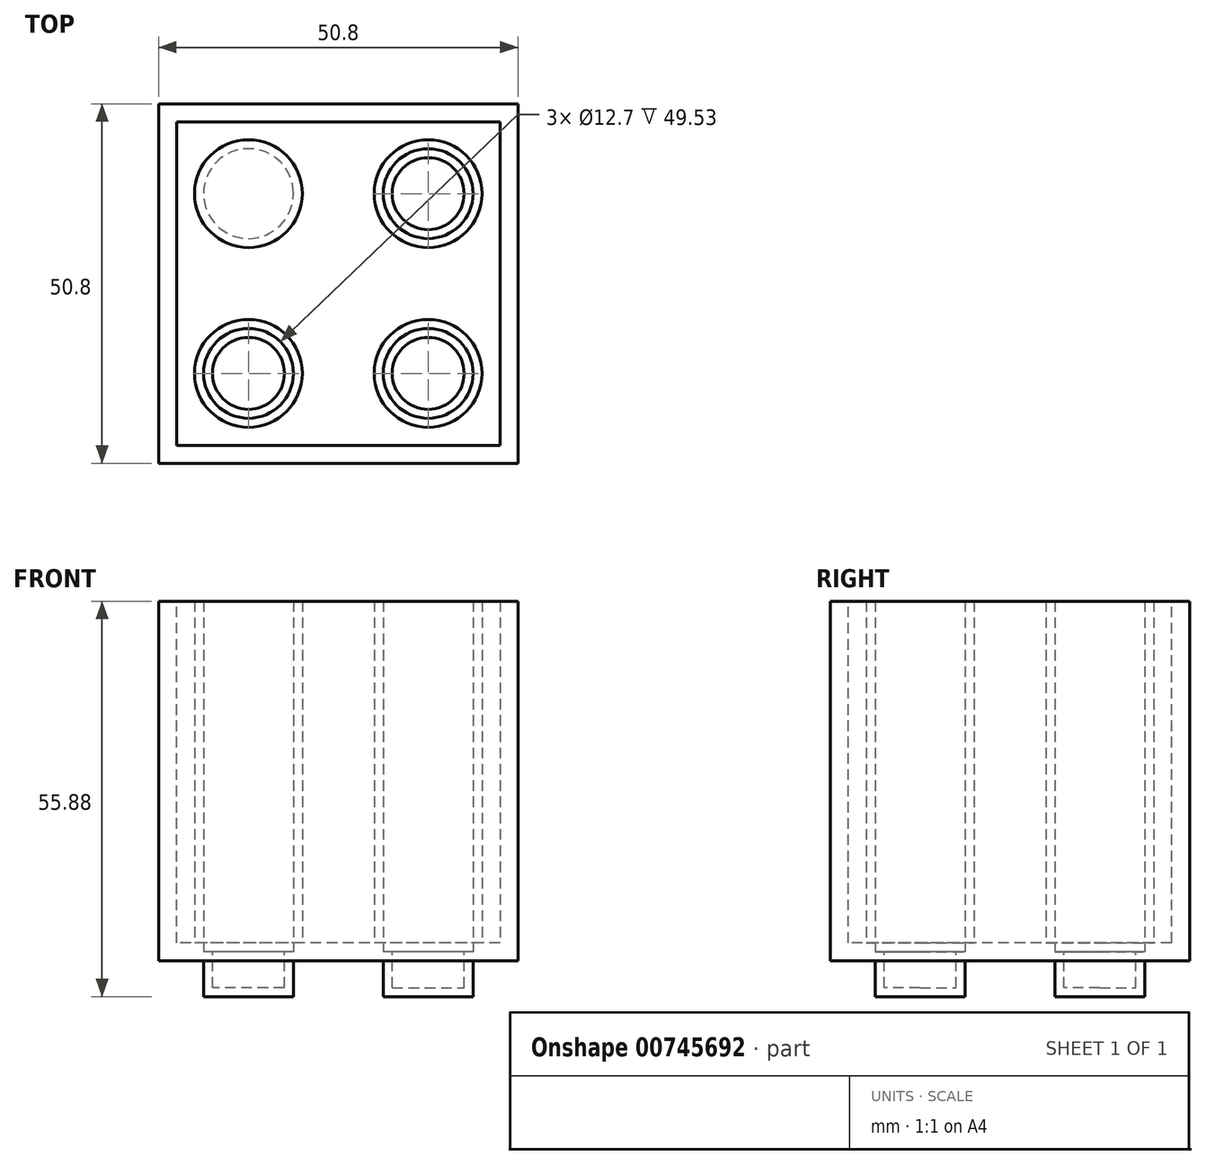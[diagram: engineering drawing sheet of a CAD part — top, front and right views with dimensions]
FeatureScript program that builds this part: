
annotation { "Feature Type Name" : "Feature", "Feature Type Description" : "" }
export const myFeature = defineFeature(function(context is Context, id is Id, definition is map)
    precondition{}
    {
        {
            var Q0;
            Q0=qCreatedBy(makeId("Front.planeOp"),FACE);
            var sketch = newSketch(context, id + "F0", { "sketchPlane" : qUnion([Q0])});
            skLineSegment(sketch, "E0", {"start": v(0, 0) * mm, "end": v(0, 50.8) * mm});
            skLineSegment(sketch, "E1", {"start": v(0, 50.8) * mm, "end": v(50.8, 50.8) * mm});
            skLineSegment(sketch, "E2", {"start": v(50.8, 50.8) * mm, "end": v(50.8, 0) * mm});
            skLineSegment(sketch, "E3", {"start": v(50.8, 0) * mm, "end": v(0, 0) * mm});
            skSolve(sketch);
        }
        {
            var Q0;
            Q0=makeQuery(id+"F0.imprint","IMPRINT",FACE,{"disambiguationData":[TD([[makeQuery(id+"F0.imprint","IMPRINT",EDGE,{"derivedFrom":sQuery(id+"F0.wireOp",EDGE,"E0")}),-1.0]])]});
            extrude(context, id + "F1", {"entities" : qUnion([Q0]), "oppositeDirection" : true, "depth" : 50.8 * mm, "offsetDistance" : 25.4 * mm});
        }
        {
            var Q0;
            Q0=makeQuery(id+"F1.opExtrude","SWEPT_FACE",FACE,{"disambiguationData":[OSD([sQuery(id+"F0.wireOp",EDGE,"E1")])]});
            shell(context, id + "F2", {"entities" : qUnion([Q0]), "thickness" : 2.54 * mm});
        }
        {
            var Q0;
            Q0=makeQuery(id+"F1.opExtrude","SWEPT_FACE",FACE,{"disambiguationData":[OSD([sQuery(id+"F0.wireOp",EDGE,"E3")])]});
            var sketch = newSketch(context, id + "F3", { "sketchPlane" : qUnion([Q0])});
            skCircle(sketch, "E4", {"center": v(12.7, -38.1) * mm, "radius": 6.35 * mm});
            skCircle(sketch, "E5", {"center": v(12.7, -12.7) * mm, "radius": 6.35 * mm});
            skCircle(sketch, "E6", {"center": v(38.1, -12.7) * mm, "radius": 6.35 * mm});
            skCircle(sketch, "E7", {"center": v(38.1, -38.1) * mm, "radius": 6.35 * mm});
            skSolve(sketch);
        }
        {
            var Q0;
            Q0 = qSketchRegion(id + "F3", true);
            extrude(context, id + "F4", {"entities" : qUnion([Q0]), "operationType" : NewBodyOperationType.ADD, "depth" : 5.08 * mm, "offsetDistance" : 25.4 * mm});
        }
        {
            var Q0;
            Q0=makeQuery(id+"F2.opShell","OFFSET_FACE",FACE,{"disambiguationData":[OSD([sQuery(id+"F0.wireOp",EDGE,"E3")])]});
            var sketch = newSketch(context, id + "F5", { "sketchPlane" : qUnion([Q0])});
            skCircle(sketch, "E8", {"center": v(12.7, 38.1) * mm, "radius": 7.62 * mm});
            skCircle(sketch, "E9", {"center": v(38.1, 38.1) * mm, "radius": 7.62 * mm});
            skCircle(sketch, "E10", {"center": v(38.1, 12.7) * mm, "radius": 7.62 * mm});
            skCircle(sketch, "E11", {"center": v(12.7, 12.7) * mm, "radius": 7.62 * mm});
            skSolve(sketch);
        }
        {
            var Q0;
            Q0 = qSketchRegion(id + "F5", true);
            extrude(context, id + "F6", {"entities" : qUnion([Q0]), "operationType" : NewBodyOperationType.ADD, "depth" : 48.26 * mm, "offsetDistance" : 25.4 * mm});
        }
        {
            var Q0;
            Q0=makeQuery(id+"F6.opExtrude","CAP_FACE",FACE,{"disambiguationData":[OSD([sQuery(id+"F5.wireOp",EDGE,"E10")])],"isStart":false});
            var Q1;
            Q1=makeQuery(id+"F6.opExtrude","CAP_FACE",FACE,{"disambiguationData":[OSD([sQuery(id+"F5.wireOp",EDGE,"E11")])],"isStart":false});
            var Q2;
            Q2=makeQuery(id+"F6.opExtrude","CAP_FACE",FACE,{"disambiguationData":[OSD([sQuery(id+"F5.wireOp",EDGE,"E8")])],"isStart":false});
            var Q3;
            Q3=makeQuery(id+"F6.opExtrude","CAP_FACE",FACE,{"disambiguationData":[OSD([sQuery(id+"F5.wireOp",EDGE,"E9")])],"isStart":false});
            shell(context, id + "F7", {"entities" : qUnion([Q0, Q1, Q2, Q3]), "thickness" : 1.27 * mm});
        }
    });
